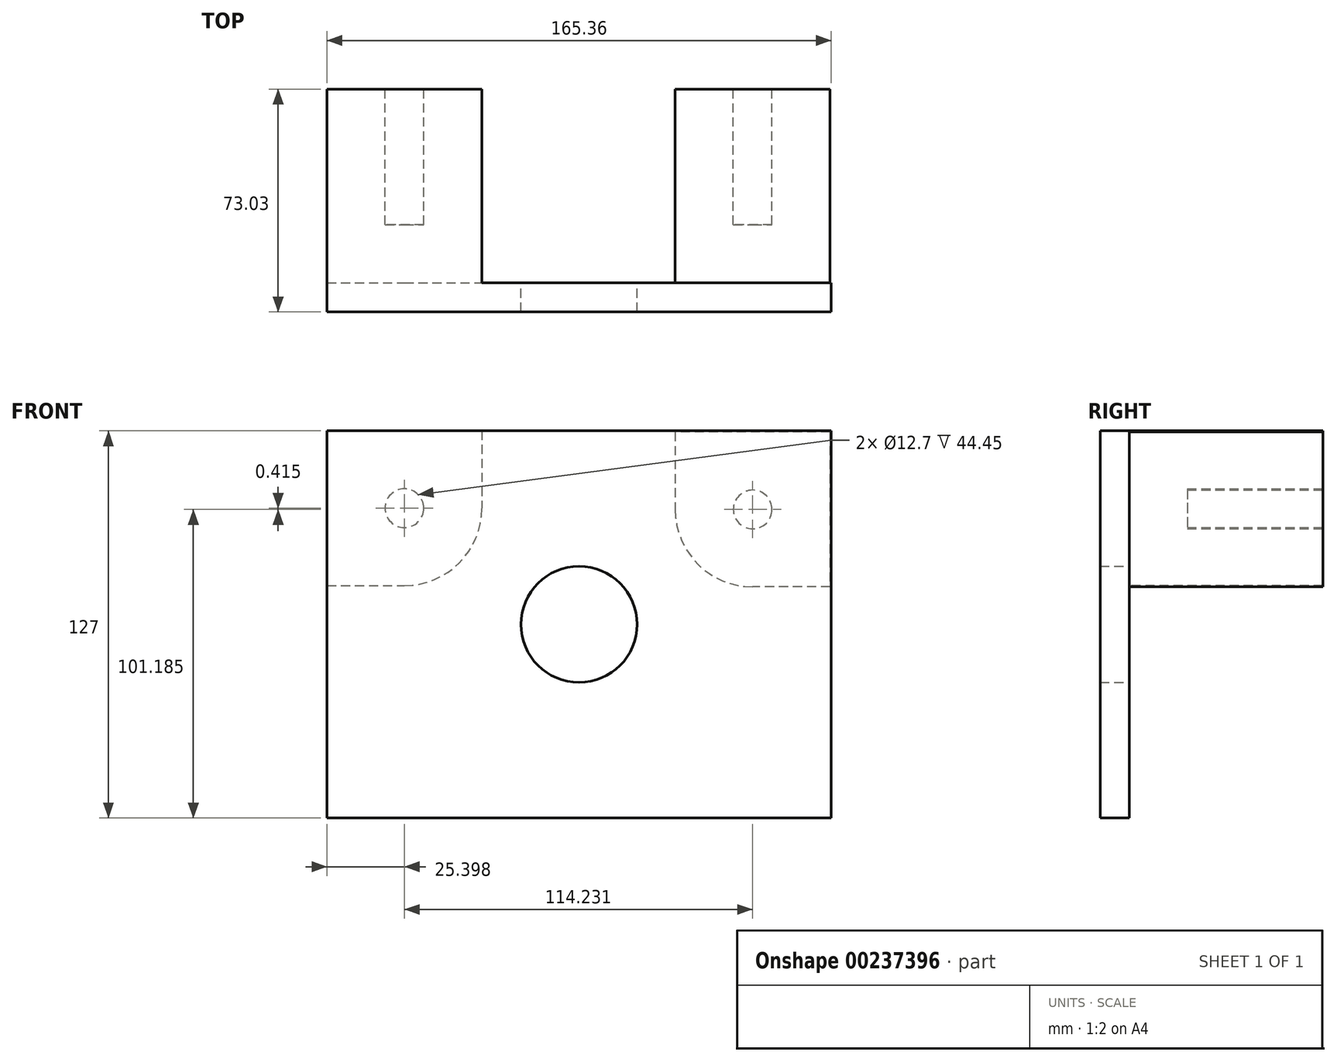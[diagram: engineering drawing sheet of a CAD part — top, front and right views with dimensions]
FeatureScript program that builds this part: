
annotation { "Feature Type Name" : "Feature", "Feature Type Description" : "" }
export const myFeature = defineFeature(function(context is Context, id is Id, definition is map)
    precondition{}
    {
        {
            var Q0;
            Q0=qCreatedBy(makeId("Front.planeOp"),FACE);
            var sketch = newSketch(context, id + "F0", { "sketchPlane" : qUnion([Q0])});
            skLineSegment(sketch, "E0.bottom", {"start": v(82.68, -63.5) * mm, "end": v(-82.68, -63.5) * mm});
            skLineSegment(sketch, "E0.top", {"start": v(82.68, 63.5) * mm, "end": v(-82.68, 63.5) * mm});
            skLineSegment(sketch, "E0.left", {"start": v(82.68, -63.5) * mm, "end": v(82.68, 63.5) * mm});
            skLineSegment(sketch, "E0.right", {"start": v(-82.68, -63.5) * mm, "end": v(-82.68, 63.5) * mm});
            skPoint(sketch, "E0.middle", {"position": v(0, 0) * mm});
            skSolve(sketch);
        }
        {
            var Q0;
            Q0=makeQuery(id+"F0.imprint","IMPRINT",FACE,{"disambiguationData":[TD([[makeQuery(id+"F0.imprint","IMPRINT",EDGE,{"derivedFrom":sQuery(id+"F0.wireOp",EDGE,"E0.bottom")}),-1.0]])]});
            extrude(context, id + "F1", {"entities" : qUnion([Q0]), "depth" : 9.52 * mm});
        }
        {
            var Q0;
            Q0=qCreatedBy(makeId("Front.planeOp"),FACE);
            var sketch = newSketch(context, id + "F2", { "sketchPlane" : qUnion([Q0])});
            skLineSegment(sketch, "E1.bottom", {"start": v(82.35, 63.08) * mm, "end": v(31.55, 63.08) * mm});
            skLineSegment(sketch, "E1.top", {"start": v(82.35, 12.28) * mm, "end": v(31.55, 12.28) * mm});
            skLineSegment(sketch, "E1.left", {"start": v(82.35, 63.08) * mm, "end": v(82.35, 12.28) * mm});
            skLineSegment(sketch, "E1.right", {"start": v(31.55, 63.08) * mm, "end": v(31.55, 12.28) * mm});
            skLineSegment(sketch, "E2.bottom", {"start": v(-82.12, 61.63) * mm, "end": v(-31.32, 61.63) * mm});
            skLineSegment(sketch, "E2.top", {"start": v(-82.12, 10.83) * mm, "end": v(-31.32, 10.83) * mm});
            skLineSegment(sketch, "E2.left", {"start": v(-82.12, 61.63) * mm, "end": v(-82.12, 10.83) * mm});
            skLineSegment(sketch, "E2.right", {"start": v(-31.32, 61.63) * mm, "end": v(-31.32, 10.83) * mm});
            skSolve(sketch);
        }
        {
            var Q0;
            Q0=makeQuery(id+"F2.imprint","IMPRINT",FACE,{"disambiguationData":[TD([[makeQuery(id+"F2.imprint","IMPRINT",EDGE,{"derivedFrom":sQuery(id+"F2.wireOp",EDGE,"E1.bottom")}),1.0]])]});
            extrude(context, id + "F3", {"entities" : qUnion([Q0]), "operationType" : NewBodyOperationType.ADD, "oppositeDirection" : true, "depth" : 63.5 * mm});
        }
        {
            var Q0;
            Q0=makeQuery(id+"F1.opExtrude","CAP_FACE",FACE,{"disambiguationData":[OSD([sQuery(id+"F0.wireOp",EDGE,"E0.bottom"),sQuery(id+"F0.wireOp",EDGE,"E0.top"),sQuery(id+"F0.wireOp",EDGE,"E0.left"),sQuery(id+"F0.wireOp",EDGE,"E0.right")])],"isStart":true});
            var sketch = newSketch(context, id + "F4", { "sketchPlane" : qUnion([Q0])});
            skLineSegment(sketch, "E3.bottom", {"start": v(82.68, 63.5) * mm, "end": v(31.88, 63.5) * mm});
            skLineSegment(sketch, "E3.top", {"start": v(82.68, 12.7) * mm, "end": v(31.88, 12.7) * mm});
            skLineSegment(sketch, "E3.left", {"start": v(82.68, 63.5) * mm, "end": v(82.68, 12.7) * mm});
            skLineSegment(sketch, "E3.right", {"start": v(31.88, 63.5) * mm, "end": v(31.88, 12.7) * mm});
            skSolve(sketch);
        }
        {
            var Q0;
            Q0 = qSketchRegion(id + "F4", true);
            extrude(context, id + "F5", {"entities" : qUnion([Q0]), "operationType" : NewBodyOperationType.ADD, "depth" : 63.5 * mm});
        }
        {
            var Q0;
            Q0=makeQuery(id+"F3.opExtrude","SWEPT_EDGE",EDGE,{"disambiguationData":[OSD([sQuery(id+"F2.wireOp",EDGE,"E1.top"),sQuery(id+"F2.wireOp",EDGE,"E1.right")])]});
            var Q1;
            Q1=makeQuery(id+"F5.opExtrude","SWEPT_EDGE",EDGE,{"disambiguationData":[OSD([sQuery(id+"F4.wireOp",EDGE,"E3.top"),sQuery(id+"F4.wireOp",EDGE,"E3.right")])]});
            fillet(context, id + "F6", {"entities" : qUnion([Q0, Q1]), "radius" : 25.4 * mm, "tangentPropagation" : true, "allowEdgeOverflow" : false});
        }
        {
            var Q0;
            Q0=qCreatedBy(makeId("Front.planeOp"),FACE);
            var sketch = newSketch(context, id + "F7", { "sketchPlane" : qUnion([Q0])});
            skCircle(sketch, "E4", {"center": v(0, 0) * mm, "radius": 19.05 * mm});
            skSolve(sketch);
        }
        {
            var Q0;
            Q0=makeQuery(id+"F7.imprint","IMPRINT",FACE,{"disambiguationData":[TD([[makeQuery(id+"F7.imprint","IMPRINT",EDGE,{"derivedFrom":sQuery(id+"F7.wireOp",EDGE,"E4")}),1.0]])]});
            extrude(context, id + "F8", {"entities" : qUnion([Q0]), "operationType" : NewBodyOperationType.REMOVE, "endBound" : BoundingType.THROUGH_ALL, "oppositeDirection" : true, "depth" : 25.4 * mm});
        }
        {
            var Q0;
            Q0=qCreatedBy(makeId("Front.planeOp"),FACE);
            var sketch = newSketch(context, id + "F9", { "sketchPlane" : qUnion([Q0])});
            skCircle(sketch, "E5", {"center": v(0, 0) * mm, "radius": 19.05 * mm});
            skSolve(sketch);
        }
        {
            var Q0;
            Q0=makeQuery(id+"F9.imprint","IMPRINT",FACE,{"disambiguationData":[TD([[makeQuery(id+"F9.imprint","IMPRINT",EDGE,{"derivedFrom":sQuery(id+"F9.wireOp",EDGE,"E5")}),1.0]])]});
            extrude(context, id + "F10", {"entities" : qUnion([Q0]), "operationType" : NewBodyOperationType.REMOVE, "endBound" : BoundingType.THROUGH_ALL, "oppositeDirection" : true, "depth" : 25.4 * mm});
        }
        {
            var Q0;
            Q0=qCreatedBy(makeId("Front.planeOp"),FACE);
            var sketch = newSketch(context, id + "F11", { "sketchPlane" : qUnion([Q0])});
            skCircle(sketch, "E6", {"center": v(0, 0) * mm, "radius": 19.05 * mm});
            skSolve(sketch);
        }
        {
            var Q0;
            Q0 = qSketchRegion(id + "F11", true);
            extrude(context, id + "F12", {"entities" : qUnion([Q0]), "operationType" : NewBodyOperationType.REMOVE, "endBound" : BoundingType.THROUGH_ALL, "depth" : 25.4 * mm});
        }
        {
            var Q0;
            Q0=makeQuery(id+"F3.opExtrude","CAP_FACE",FACE,{"disambiguationData":[OSD([sQuery(id+"F2.wireOp",EDGE,"E1.bottom"),sQuery(id+"F2.wireOp",EDGE,"E1.top"),sQuery(id+"F2.wireOp",EDGE,"E1.left"),sQuery(id+"F2.wireOp",EDGE,"E1.right")])],"isStart":false});
            var sketch = newSketch(context, id + "F13", { "sketchPlane" : qUnion([Q0])});
            skCircle(sketch, "E7", {"center": v(-56.95, 37.68) * mm, "radius": 6.35 * mm});
            skCircle(sketch, "E8", {"center": v(57.28, 38.1) * mm, "radius": 6.35 * mm});
            skSolve(sketch);
        }
        {
            var Q0;
            Q0=makeQuery(id+"F13.imprint","IMPRINT",FACE,{"disambiguationData":[TD([[makeQuery(id+"F13.imprint","IMPRINT",EDGE,{"derivedFrom":sQuery(id+"F13.wireOp",EDGE,"E7")}),1.0]])]});
            var Q1;
            Q1=makeQuery(id+"F13.imprint","IMPRINT",FACE,{"disambiguationData":[TD([[makeQuery(id+"F13.imprint","IMPRINT",EDGE,{"derivedFrom":sQuery(id+"F13.wireOp",EDGE,"E8")}),1.0]])]});
            extrude(context, id + "F14", {"entities" : qUnion([Q0, Q1]), "operationType" : NewBodyOperationType.REMOVE, "oppositeDirection" : true, "depth" : 44.45 * mm});
        }
    });
